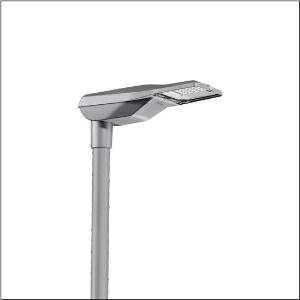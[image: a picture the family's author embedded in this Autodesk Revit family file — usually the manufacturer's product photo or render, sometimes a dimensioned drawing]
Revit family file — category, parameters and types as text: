
# Revit family: streetlight_sl_21_iq_micro___stw1_0a_5xe1e21g08cb_2b52
name_source: partatom
category: Lighting Fixtures
units: mm (PartAtom-declared; Revit-internal decimal feet)

## family parameters
Cut with Voids When Loaded = No
Host = Face
Light Source = No
Part Type = Normal
Room Calculation Point = No
Round Connector Dimension = Use Diameter
Shared = No

## types (1)
- --- (1 x LED, 2380 lm, 19.4 W, 2200K)
    Apparent Load = 19 VA
    CIE Flux Codes = 38 75 98 100 100
    Color Rendering = 70
    Color Temperature = 2200K
    Default Elevation = 1800 mm
    Description = Streetlight SL 21 iQ micro, mast luminaire, primary light control with lens, of PMMA, primary optical cover: cover, of toughened safety glass, transparent, light distribution: STW1.0a, light emission: direct distribution, primary light characteristic: asymmetric, installation type: post-top, side-entry, LED, High Power LED, rated luminous flux: 2.380lm, luminous efficacy: 123lm/W, light colour: 722, colour temperature: 2200K, control: Street-Remote, Auto-Match, Temp-Guard, Lumen-Switch, Night-Set, Smart-Wire, Light-Fading, Desk-Remote (wireless, voltage-free reading and setting of iQ features in the workshop via application-optimized NFC function/RFID function), optimised constant luminous flux control (CLO 2.0), presetting dimming linear, mains connection: 220..240V, AC, 50/60Hz, start of lifetime: 19W, end of service life: 20W, reduction: 10W, luminaire housing, of diecast aluminium, powder-coated, Siteco® metallic grey (DB 702S), corrosivity category C5 mid according to DIN EN ISO 12944, please order mast flange separately, inclination adjustable: 0°, 5°, 10°, 15°, sealing non-destructively replaceable, multi-level sealing system, length: 528mm, width: 235mm, height: 110mm, mast flange for spigot size: 42mm (side-entry): 5XC10008XM4, 60/48mm (side-entry/post-top): 5XC10108XM2, 76/60mm (side-entry/post-top): 5XC10108XM1, protection rating (complete): IP66, insulation class (complete): insulation class II (safety insulation), certification: CE, ENEC, ENEC+, VDE, impact resistance: IK09, permissible operating ambient temperature for outdoor applications: -40..+50°C, standard-compliant lighting for roads and squares, packaging unit: 1 piece

Light Distribution: STW1.0a
    Height = 110 mm
    Lamp = 1 x LED
    Lamp Light Flux = 2380 lm
    Lamp Power = 19.4 W
    Lamp count = 1
    Length = 528 mm
    Luminous efficacy = 123 lm/W
    Manufacturer = Siteco
    ModVariant = No
    Model = 5XE1E21G08CB
    Number of Poles = 1
    OnlyDefault = Yes
    Power Factor = 1
    Product Name = Streetlight SL 21 iQ micro | STW1.0a
    Product group = mast luminaire | pylon top
    ProductGroupID = 6100
    Protection Class = Protection class II
    Protection Degree = IP 66
    RLX_Detail_Level = 1
    RLX_Emergency_Light_Flux = 0 lm
    RLX_Emergency_Type = 0
    RLX_Emergency_Type_DB = No
    RlxData = <blob elided: 98609 chars, md5=7ed9b712>
    Socket = socket
    Standby Power = 0 W
    System Light Flux = 2380 lm
    System Power = 19 W
    Type Comments = factory setting: luminous flux: 100 % | dim-lin: 254 | 387 mA
    Type Image = l_1006881.jpg
    URL = http://relux.com
    VarID = @adj_070257
    Voltage = 0 V
    Weight = 0.00 kg
    Width = 235 mm

## geometry (parser evidence)
native form markers: Blend x4, Sweep x9
no freeform markers — native parametric forms only
